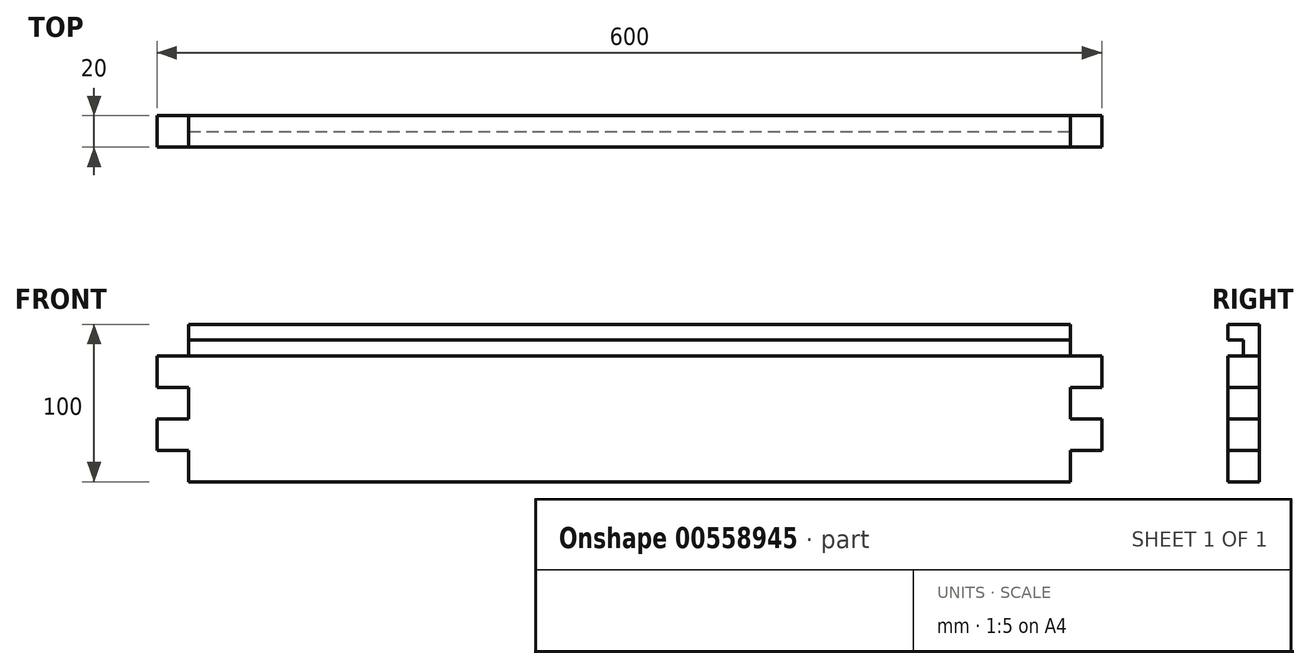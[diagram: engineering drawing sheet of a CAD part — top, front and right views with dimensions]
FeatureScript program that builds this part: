
annotation { "Feature Type Name" : "Feature", "Feature Type Description" : "" }
export const myFeature = defineFeature(function(context is Context, id is Id, definition is map)
    precondition{}
    {
        {
            var Q0;
            Q0=qCreatedBy(makeId("Front.planeOp"),FACE);
            var sketch = newSketch(context, id + "F0", { "sketchPlane" : qUnion([Q0])});
            skLineSegment(sketch, "E0.bottom", {"start": v(300, -50) * mm, "end": v(-300, -50) * mm});
            skLineSegment(sketch, "E0.top", {"start": v(300, 50) * mm, "end": v(-300, 50) * mm});
            skLineSegment(sketch, "E0.left", {"start": v(300, -50) * mm, "end": v(300, 50) * mm});
            skLineSegment(sketch, "E0.right", {"start": v(-300, -50) * mm, "end": v(-300, 50) * mm});
            skPoint(sketch, "E0.middle", {"position": v(0, 0) * mm});
            skSolve(sketch);
        }
        {
            var Q0;
            Q0=makeQuery(id+"F0.imprint","IMPRINT",FACE,{"disambiguationData":[TD([[makeQuery(id+"F0.imprint","IMPRINT",EDGE,{"derivedFrom":sQuery(id+"F0.wireOp",EDGE,"E0.bottom")}),-1.0]])]});
            extrude(context, id + "F1", {"entities" : qUnion([Q0]), "depth" : 20 * mm, "offsetDistance" : 25 * mm});
        }
        {
            var Q0;
            Q0=makeQuery(id+"F1.opExtrude","CAP_FACE",FACE,{"disambiguationData":[OSD([sQuery(id+"F0.wireOp",EDGE,"E0.bottom"),sQuery(id+"F0.wireOp",EDGE,"E0.top"),sQuery(id+"F0.wireOp",EDGE,"E0.left"),sQuery(id+"F0.wireOp",EDGE,"E0.right")])],"isStart":true});
            var sketch = newSketch(context, id + "F2", { "sketchPlane" : qUnion([Q0])});
            skLineSegment(sketch, "E1.bottom", {"start": v(-300, -50) * mm, "end": v(-280, -50) * mm});
            skLineSegment(sketch, "E1.top", {"start": v(-300, -30) * mm, "end": v(-280, -30) * mm});
            skLineSegment(sketch, "E1.left", {"start": v(-300, -50) * mm, "end": v(-300, -30) * mm});
            skLineSegment(sketch, "E1.right", {"start": v(-280, -50) * mm, "end": v(-280, -30) * mm});
            skLineSegment(sketch, "E2.bottom", {"start": v(-300, -10) * mm, "end": v(-280, -10) * mm});
            skLineSegment(sketch, "E2.top", {"start": v(-300, 10) * mm, "end": v(-280, 10) * mm});
            skLineSegment(sketch, "E2.left", {"start": v(-300, -10) * mm, "end": v(-300, 10) * mm});
            skLineSegment(sketch, "E2.right", {"start": v(-280, -10) * mm, "end": v(-280, 10) * mm});
            skLineSegment(sketch, "E3.MirrorCS", {"start": v(300, -10) * mm, "end": v(300, 10) * mm});
            skLineSegment(sketch, "E4.MirrorCS", {"start": v(300, 10) * mm, "end": v(280, 10) * mm});
            skLineSegment(sketch, "E5.MirrorCS", {"start": v(300, -10) * mm, "end": v(280, -10) * mm});
            skLineSegment(sketch, "E6.MirrorCS", {"start": v(280, -50) * mm, "end": v(280, -30) * mm});
            skLineSegment(sketch, "E7.MirrorCS", {"start": v(300, -50) * mm, "end": v(300, -30) * mm});
            skLineSegment(sketch, "E8.MirrorCS", {"start": v(300, -30) * mm, "end": v(280, -30) * mm});
            skLineSegment(sketch, "E9.MirrorCS", {"start": v(280, -10) * mm, "end": v(280, 10) * mm});
            skLineSegment(sketch, "E10.MirrorCS", {"start": v(300, -50) * mm, "end": v(280, -50) * mm});
            skLineSegment(sketch, "E11.bottom", {"start": v(300, 30) * mm, "end": v(280, 30) * mm});
            skLineSegment(sketch, "E11.top", {"start": v(300, 50) * mm, "end": v(280, 50) * mm});
            skLineSegment(sketch, "E11.left", {"start": v(300, 30) * mm, "end": v(300, 50) * mm});
            skLineSegment(sketch, "E11.right", {"start": v(280, 30) * mm, "end": v(280, 50) * mm});
            skLineSegment(sketch, "E12.MirrorCS", {"start": v(-300, 30) * mm, "end": v(-280, 30) * mm});
            skLineSegment(sketch, "E13.MirrorCS", {"start": v(-300, 30) * mm, "end": v(-300, 50) * mm});
            skLineSegment(sketch, "E14.MirrorCS", {"start": v(-300, 50) * mm, "end": v(-280, 50) * mm});
            skLineSegment(sketch, "E15.MirrorCS", {"start": v(-280, 30) * mm, "end": v(-280, 50) * mm});
            skSolve(sketch);
        }
        {
            var Q0;
            Q0 = qSketchRegion(id + "F2", true);
            extrude(context, id + "F3", {"entities" : qUnion([Q0]), "operationType" : NewBodyOperationType.REMOVE, "endBound" : BoundingType.UP_TO_NEXT, "oppositeDirection" : true, "depth" : 25 * mm, "offsetDistance" : 25 * mm});
        }
        {
            var Q0;
            Q0=makeQuery(id+"F1.opExtrude","CAP_FACE",FACE,{"disambiguationData":[OSD([sQuery(id+"F0.wireOp",EDGE,"E0.bottom"),sQuery(id+"F0.wireOp",EDGE,"E0.top"),sQuery(id+"F0.wireOp",EDGE,"E0.left"),sQuery(id+"F0.wireOp",EDGE,"E0.right")])],"isStart":false});
            var sketch = newSketch(context, id + "F4", { "sketchPlane" : qUnion([Q0])});
            skLineSegment(sketch, "E16.bottom", {"start": v(300, 30) * mm, "end": v(-300, 30) * mm});
            skLineSegment(sketch, "E16.top", {"start": v(300, 40) * mm, "end": v(-300, 40) * mm});
            skLineSegment(sketch, "E16.left", {"start": v(300, 30) * mm, "end": v(300, 40) * mm});
            skLineSegment(sketch, "E16.right", {"start": v(-300, 30) * mm, "end": v(-300, 40) * mm});
            skPoint(sketch, "E16.middle", {"position": v(0, 35) * mm});
            skSolve(sketch);
        }
        {
            var Q0;
            Q0 = qSketchRegion(id + "F4", true);
            extrude(context, id + "F5", {"entities" : qUnion([Q0]), "operationType" : NewBodyOperationType.REMOVE, "oppositeDirection" : true, "depth" : 10 * mm, "offsetDistance" : 25 * mm});
        }
    });
